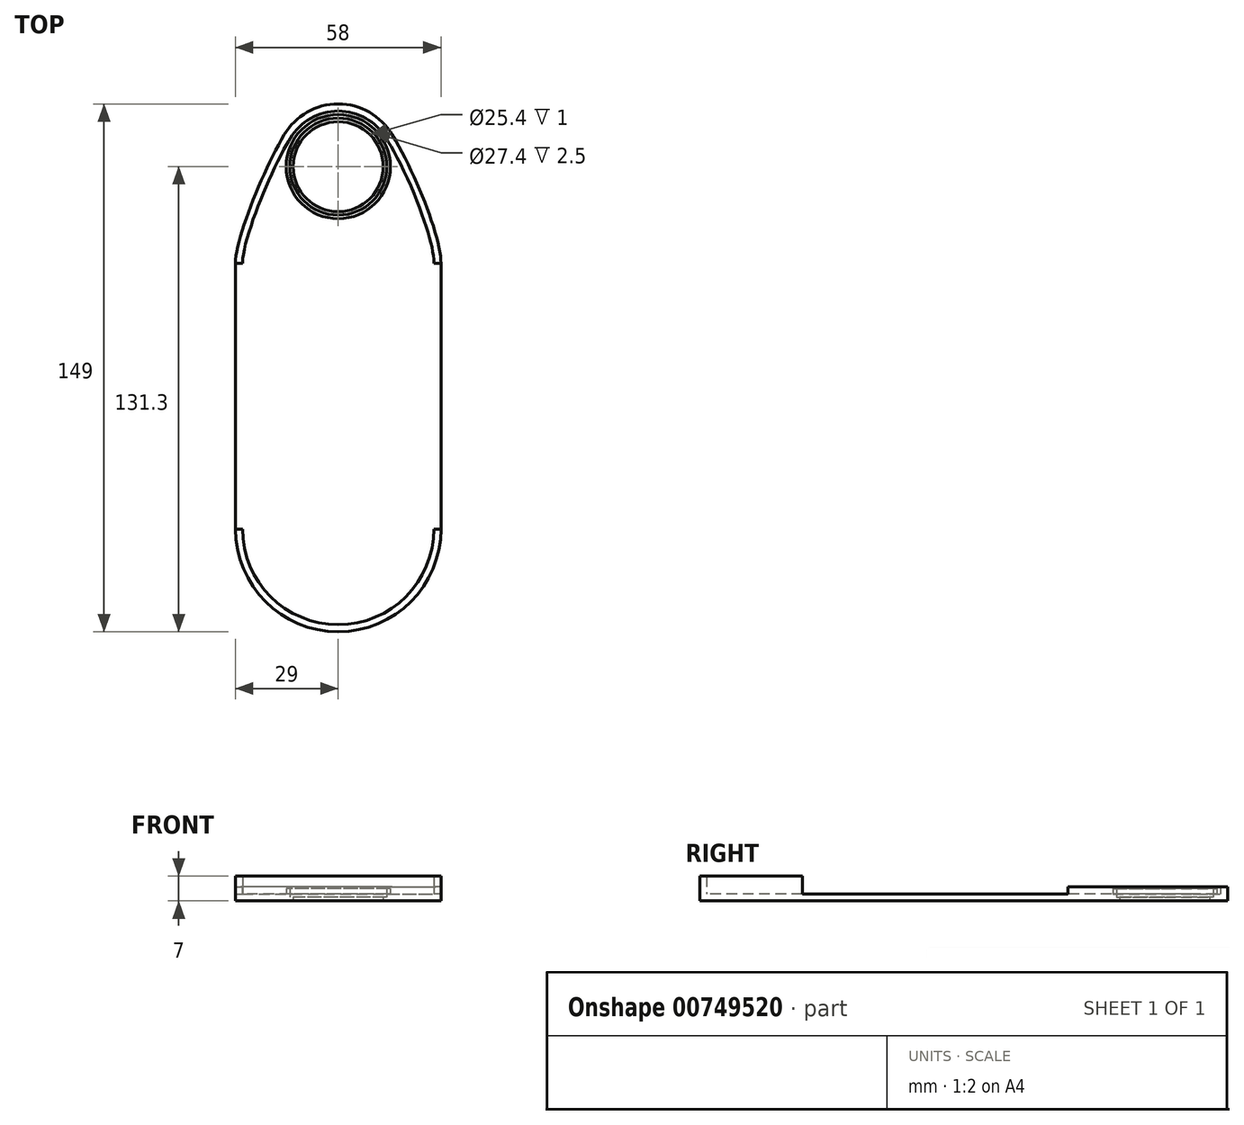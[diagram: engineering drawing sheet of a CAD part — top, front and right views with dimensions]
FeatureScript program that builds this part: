
annotation { "Feature Type Name" : "Feature", "Feature Type Description" : "" }
export const myFeature = defineFeature(function(context is Context, id is Id, definition is map)
    precondition{}
    {
        {
            var Q0;
            Q0=qCreatedBy(makeId("Top.planeOp"),FACE);
            var sketch = newSketch(context, id + "F0", { "sketchPlane" : qUnion([Q0])});
            skArc(sketch, "E0", {"start": v(-29, -45) * mm, "mid": v(0, -74) * mm, "end": v(29, -45) * mm});
            skLineSegment(sketch, "E1", {"start": v(-29, -45) * mm, "end": v(-29, 30) * mm});
            skLineSegment(sketch, "E2", {"start": v(29, -45) * mm, "end": v(29, 30) * mm});
            skArc(sketch, "E3", {"start": v(15.25, 66.28) * mm, "mid": v(0, 75) * mm, "end": v(-15.25, 66.28) * mm});
            skCircle(sketch, "E4", {"center": v(0, 57.3) * mm, "radius": 12.7 * mm});
            skFitSpline(sketch, "E5", {"points": [v(-15.25, 66.28) * mm, v(-29, 30) * mm], "startDerivative": vector(-17.92, -30.43) * mm, "endDerivative": vector(0, -21.56) * mm});
            skFitSpline(sketch, "E6", {"points": [v(15.25, 66.28) * mm, v(29, 30) * mm], "startDerivative": vector(21.03, -35.71) * mm, "endDerivative": vector(0, -21.56) * mm});
            skLineSegment(sketch, "E7", {"start": v(-27, 30) * mm, "end": v(-29, 30) * mm});
            skLineSegment(sketch, "E8", {"start": v(27, 30) * mm, "end": v(29, 30) * mm});
            skLineSegment(sketch, "E9", {"start": v(-29, -45) * mm, "end": v(-27, -45) * mm});
            skLineSegment(sketch, "E10", {"start": v(27, -45) * mm, "end": v(29, -45) * mm});
            skSolve(sketch);
        }
        {
            var Q0;
            Q0=makeQuery(id+"F0.imprint","IMPRINT",FACE,{"disambiguationData":[TD([[makeQuery(id+"F0.imprint","IMPRINT",EDGE,{"derivedFrom":sQuery(id+"F0.wireOp",EDGE,"87762f92-a82d-4736-8b2d-cb61234f6977.0")}),1.0]])]});
            var Q1;
            Q1=makeQuery(id+"F0.imprint","IMPRINT",FACE,{"disambiguationData":[TD([[makeQuery(id+"F0.imprint","IMPRINT",EDGE,{"derivedFrom":sQuery(id+"F0.wireOp",EDGE,"E1")}),-1.0]])]});
            var Q2;
            Q2=makeQuery(id+"F0.imprint","IMPRINT",FACE,{"disambiguationData":[TD([[makeQuery(id+"F0.imprint","IMPRINT",EDGE,{"derivedFrom":sQuery(id+"F0.wireOp",EDGE,"E2")}),1.0]])]});
            extrude(context, id + "F1", {"entities" : qUnion([Q0, Q1, Q2]), "depth" : 2 * mm, "offsetDistance" : 25 * mm});
        }
        {
            var Q0;
            Q0=makeQuery(id+"F1.opExtrude","CAP_FACE",FACE,{"disambiguationData":[OSD([sQuery(id+"F0.wireOp",EDGE,"E1"),sQuery(id+"F0.wireOp",EDGE,"E2"),sQuery(id+"F0.wireOp",EDGE,"E4"),sQuery(id+"F0.wireOp",EDGE,"87762f92-a82d-4736-8b2d-cb61234f6977.0"),sQuery(id+"F0.wireOp",EDGE,"87762f92-a82d-4736-8b2d-cb61234f6977.2"),sQuery(id+"F0.wireOp",EDGE,"87762f92-a82d-4736-8b2d-cb61234f6977.3"),sQuery(id+"F0.wireOp",EDGE,"87762f92-a82d-4736-8b2d-cb61234f6977.5"),sQuery(id+"F0.wireOp",EDGE,"E7"),sQuery(id+"F0.wireOp",EDGE,"E8"),sQuery(id+"F0.wireOp",EDGE,"E9"),sQuery(id+"F0.wireOp",EDGE,"E10")])],"isStart":false});
            var sketch = newSketch(context, id + "F2", { "sketchPlane" : qUnion([Q0])});
            skCircle(sketch, "E11", {"center": v(0, 57.3) * mm, "radius": 13.7 * mm});
            skCircle(sketch, "E12", {"center": v(0, 57.3) * mm, "radius": 14.7 * mm});
            skSolve(sketch);
        }
        {
            var Q0;
            Q0=makeQuery(id+"F2.imprint","IMPRINT",FACE,{"disambiguationData":[TD([[makeQuery(id+"F2.imprint","IMPRINT",EDGE,{"derivedFrom":sQuery(id+"F2.wireOp",EDGE,"E11")}),-1.0]])]});
            extrude(context, id + "F3", {"entities" : qUnion([Q0]), "operationType" : NewBodyOperationType.ADD, "depth" : 1.5 * mm, "offsetDistance" : 25 * mm});
        }
        {
            var Q0;
            {var subQ0=sQuery(id+"F0.wireOp",EDGE,"E4");Q0=makeQuery(id+"F3.boolean.opBoolean","SPLIT",FACE,{"disambiguationData":[TD([makeQuery(id+"F1.opExtrude","SWEPT_FACE",FACE,{"disambiguationData":[OSD([subQ0])]})])],"derivedFrom":makeQuery(id+"F1.opExtrude","CAP_FACE",FACE,{"disambiguationData":[OSD([sQuery(id+"F0.wireOp",EDGE,"E1"),sQuery(id+"F0.wireOp",EDGE,"E2"),subQ0,sQuery(id+"F0.wireOp",EDGE,"87762f92-a82d-4736-8b2d-cb61234f6977.0"),sQuery(id+"F0.wireOp",EDGE,"87762f92-a82d-4736-8b2d-cb61234f6977.2"),sQuery(id+"F0.wireOp",EDGE,"87762f92-a82d-4736-8b2d-cb61234f6977.3"),sQuery(id+"F0.wireOp",EDGE,"87762f92-a82d-4736-8b2d-cb61234f6977.5"),sQuery(id+"F0.wireOp",EDGE,"E7"),sQuery(id+"F0.wireOp",EDGE,"E8"),sQuery(id+"F0.wireOp",EDGE,"E9"),sQuery(id+"F0.wireOp",EDGE,"E10")])],"isStart":false})});}
            extrude(context, id + "F4", {"entities" : qUnion([Q0]), "operationType" : NewBodyOperationType.REMOVE, "oppositeDirection" : true, "depth" : 1 * mm, "offsetDistance" : 25 * mm});
        }
        {
            var Q0;
            {var subQ0=sQuery(id+"F0.wireOp",EDGE,"E2");var subQ1=sQuery(id+"F0.wireOp",EDGE,"E1");var subQ2=sQuery(id+"F0.wireOp",EDGE,"E3");var subQ3=sQuery(id+"F0.wireOp",EDGE,"E0");var subQ4=sQuery(id+"F0.wireOp",EDGE,"E5");var subQ5=sQuery(id+"F0.wireOp",EDGE,"E6");Q0=makeQuery(id+"F3.boolean.opBoolean","SPLIT",FACE,{"disambiguationData":[TD([makeQuery(id+"F1.opExtrude","SWEPT_FACE",FACE,{"disambiguationData":[OSD([subQ3])]})])],"derivedFrom":makeQuery(id+"F1.opExtrude","CAP_FACE",FACE,{"disambiguationData":[OSD([subQ3,subQ1,subQ0,subQ2,sQuery(id+"F0.wireOp",EDGE,"E4"),subQ4,subQ5])],"isStart":false})});}
            var sketch = newSketch(context, id + "F5", { "sketchPlane" : qUnion([Q0])});
            skArc(sketch, "E13.0", {"start": v(13.53, 65.27) * mm, "mid": v(0, 73) * mm, "end": v(-13.53, 65.27) * mm});
            skLineSegment(sketch, "E13.1", {"start": v(-27, -45) * mm, "end": v(-27, 30) * mm});
            skArc(sketch, "E13.2", {"start": v(-27, -45) * mm, "mid": v(0, -72) * mm, "end": v(27, -45) * mm});
            skFitSpline(sketch, "E13.3", {"points": [v(-13.53, 65.27) * mm, v(-14.25, 64.04) * mm, v(-15.77, 61.28) * mm, v(-18.12, 56.55) * mm, v(-20.42, 51.46) * mm, v(-22.55, 46.28) * mm, v(-24.4, 41.25) * mm, v(-25.85, 36.62) * mm, v(-26.63, 33.33) * mm, v(-26.95, 31.21) * mm, v(-27, 30.36) * mm, v(-27, 30) * mm]});
            skLineSegment(sketch, "E13.4", {"start": v(27, -45) * mm, "end": v(27, 30) * mm});
            skFitSpline(sketch, "E13.5", {"points": [v(13.53, 65.27) * mm, v(15.25, 62.35) * mm, v(18.67, 55.84) * mm, v(22.37, 47.22) * mm, v(24.67, 40.8) * mm, v(25.98, 36.41) * mm, v(26.68, 33.28) * mm, v(26.96, 31.22) * mm, v(27, 30.37) * mm, v(27, 30) * mm]});
            skLineSegment(sketch, "E14", {"start": v(29, 30) * mm, "end": v(27, 30) * mm});
            skLineSegment(sketch, "E15", {"start": v(29, -45) * mm, "end": v(27, -45) * mm});
            skLineSegment(sketch, "E16", {"start": v(-29, 30) * mm, "end": v(-27, 30) * mm});
            skLineSegment(sketch, "E17", {"start": v(-29, -45) * mm, "end": v(-27, -45) * mm});
            skSolve(sketch);
        }
        {
            var Q0;
            Q0=makeQuery(id+"F5.imprint","IMPRINT",FACE,{"disambiguationData":[TD([[makeQuery(id+"F5.imprint","IMPRINT",EDGE,{"derivedFrom":sQuery(id+"F5.wireOp",EDGE,"E13.2")}),-1.0]])]});
            extrude(context, id + "F6", {"entities" : qUnion([Q0]), "operationType" : NewBodyOperationType.ADD, "depth" : 5 * mm, "offsetDistance" : 25 * mm});
        }
        {
            var Q0;
            Q0=makeQuery(id+"F5.imprint","IMPRINT",FACE,{"disambiguationData":[TD([[makeQuery(id+"F5.imprint","IMPRINT",EDGE,{"derivedFrom":sQuery(id+"F5.wireOp",EDGE,"E13.0")}),-1.0]])]});
            extrude(context, id + "F7", {"entities" : qUnion([Q0]), "operationType" : NewBodyOperationType.ADD, "depth" : 2 * mm, "offsetDistance" : 25 * mm});
        }
    });
